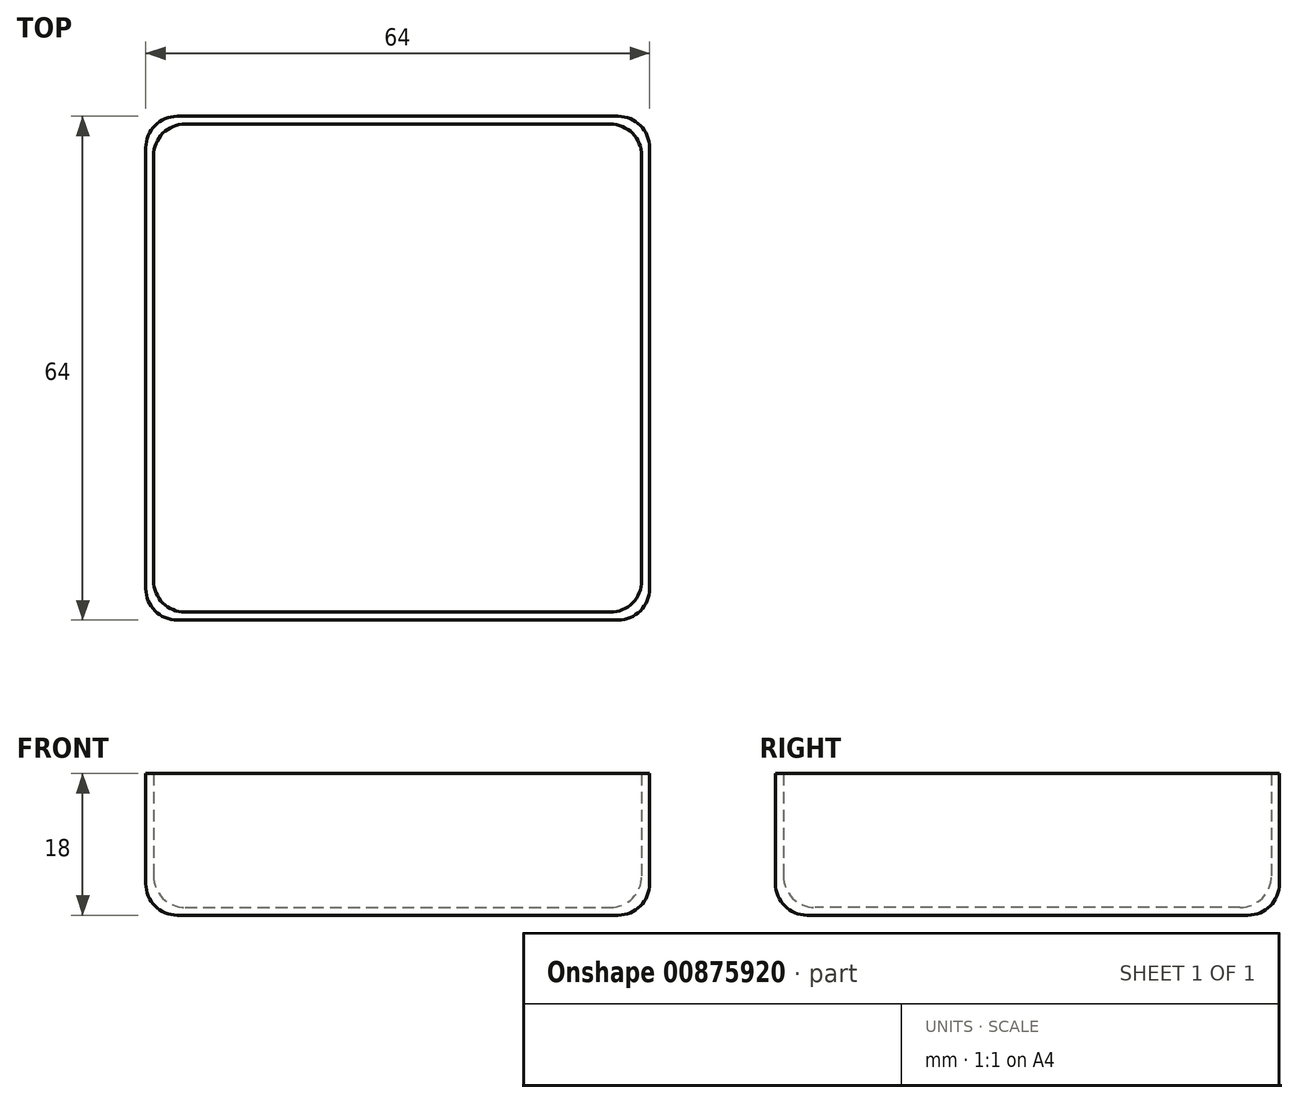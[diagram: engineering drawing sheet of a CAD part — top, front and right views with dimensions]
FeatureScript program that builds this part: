
annotation { "Feature Type Name" : "Feature", "Feature Type Description" : "" }
export const myFeature = defineFeature(function(context is Context, id is Id, definition is map)
    precondition{}
    {
        {
            assignVariable(context, id + "F0", {"name" : "wall", "anyValue" : 1});
        }
        {
            assignVariable(context, id + "F1", {"name" : "radius", "anyValue" : 4});
        }
        {
            var Q0;
            Q0=qCreatedBy(makeId("Top.planeOp"),FACE);
            var sketch = newSketch(context, id + "F2", { "sketchPlane" : qUnion([Q0])});
            skLineSegment(sketch, "E0.bottom", {"start": v(0, 0) * mm, "end": v(62, 0) * mm});
            skLineSegment(sketch, "E0.top", {"start": v(0, -62) * mm, "end": v(62, -62) * mm});
            skLineSegment(sketch, "E0.left", {"start": v(0, 0) * mm, "end": v(0, -62) * mm});
            skLineSegment(sketch, "E0.right", {"start": v(62, 0) * mm, "end": v(62, -62) * mm});
            skLineSegment(sketch, "E1.0", {"start": v(-1, 1) * mm, "end": v(-1, -63) * mm});
            skLineSegment(sketch, "E1.1", {"start": v(-1, 1) * mm, "end": v(63, 1) * mm});
            skLineSegment(sketch, "E1.2", {"start": v(63, 1) * mm, "end": v(63, -63) * mm});
            skLineSegment(sketch, "E1.3", {"start": v(-1, -63) * mm, "end": v(63, -63) * mm});
            skSolve(sketch);
        }
        {
            var Q0;
            Q0=makeQuery(id+"F2.imprint","IMPRINT",FACE,{"disambiguationData":[TD([[makeQuery(id+"F2.imprint","IMPRINT",EDGE,{"derivedFrom":sQuery(id+"F2.wireOp",EDGE,"E0.bottom")}),1.0]])]});
            var Q1;
            Q1=sQuery(id+"F2.wireOp",EDGE,"E0.right");
            var Q2;
            Q2=sQuery(id+"F2.wireOp",EDGE,"E0.left");
            var Q3;
            Q3=sQuery(id+"F2.wireOp",EDGE,"E0.bottom");
            var Q4;
            Q4=sQuery(id+"F2.wireOp",EDGE,"E0.top");
            extrude(context, id + "F3", {"entities" : qUnion([Q0]), "surfaceEntities" : qUnion([Q1, Q2, Q3, Q4]), "depth" : (18 - getVariable(context, 'wall')) * mm, "offsetDistance" : 25 * mm});
        }
        {
            var Q0;
            Q0=makeQuery(id+"F2.imprint","IMPRINT",FACE,{"disambiguationData":[TD([[makeQuery(id+"F2.imprint","IMPRINT",EDGE,{"derivedFrom":sQuery(id+"F2.wireOp",EDGE,"E0.bottom")}),-1.0]])]});
            var Q1;
            Q1=makeQuery(id+"F2.imprint","IMPRINT",FACE,{"disambiguationData":[TD([[makeQuery(id+"F2.imprint","IMPRINT",EDGE,{"derivedFrom":sQuery(id+"F2.wireOp",EDGE,"E0.bottom")}),1.0]])]});
            extrude(context, id + "F4", {"entities" : qUnion([Q0, Q1]), "operationType" : NewBodyOperationType.ADD, "oppositeDirection" : true, "depth" : (getVariable(context, 'wall')) * mm, "offsetDistance" : 25 * mm});
        }
        {
            var Q0;
            Q0=makeQuery(id+"F4.opExtrude","CAP_FACE",FACE,{"disambiguationData":[OSD([sQuery(id+"F2.wireOp",EDGE,"E1.0"),sQuery(id+"F2.wireOp",EDGE,"E1.1"),sQuery(id+"F2.wireOp",EDGE,"E1.2"),sQuery(id+"F2.wireOp",EDGE,"E1.3")])],"isStart":true});
            var Q1;
            Q1=makeQuery(id+"F4.opExtrude","CAP_FACE",FACE,{"disambiguationData":[OSD([sQuery(id+"F2.wireOp",EDGE,"E1.0"),sQuery(id+"F2.wireOp",EDGE,"E1.1"),sQuery(id+"F2.wireOp",EDGE,"E1.2"),sQuery(id+"F2.wireOp",EDGE,"E1.3")])],"isStart":false});
            var Q2;
            Q2=makeQuery(id+"F3.opExtrude","SWEPT_EDGE",EDGE,{"disambiguationData":[OSD([sQuery(id+"F2.wireOp",EDGE,"E0.top"),sQuery(id+"F2.wireOp",EDGE,"E0.left")])]});
            var Q3;
            Q3=makeQuery(id+"F3.opExtrude","SWEPT_EDGE",EDGE,{"disambiguationData":[OSD([sQuery(id+"F2.wireOp",EDGE,"E0.bottom"),sQuery(id+"F2.wireOp",EDGE,"E0.left")])]});
            var Q4;
            Q4=makeQuery(id+"F3.opExtrude","SWEPT_EDGE",EDGE,{"disambiguationData":[OSD([sQuery(id+"F2.wireOp",EDGE,"E0.bottom"),sQuery(id+"F2.wireOp",EDGE,"E0.right")])]});
            var Q5;
            Q5=makeQuery(id+"F3.opExtrude","SWEPT_EDGE",EDGE,{"disambiguationData":[OSD([sQuery(id+"F2.wireOp",EDGE,"E0.top"),sQuery(id+"F2.wireOp",EDGE,"E0.right")])]});
            var Q6;
            {var subQ0=sQuery(id+"F2.wireOp",EDGE,"E1.1");var subQ1=sQuery(id+"F2.wireOp",EDGE,"E1.0");Q6=makeQuery(id+"F4.boolean.opBoolean","MERGE",EDGE,{"derivedFrom":[makeQuery(id+"F3.opExtrude","SWEPT_EDGE",EDGE,{"disambiguationData":[OSD([subQ1,subQ0])]}),makeQuery(id+"F4.opExtrude","SWEPT_EDGE",EDGE,{"disambiguationData":[OSD([subQ1,subQ0])]})]});}
            var Q7;
            {var subQ0=sQuery(id+"F2.wireOp",EDGE,"E1.2");var subQ1=sQuery(id+"F2.wireOp",EDGE,"E1.1");Q7=makeQuery(id+"F4.boolean.opBoolean","MERGE",EDGE,{"derivedFrom":[makeQuery(id+"F3.opExtrude","SWEPT_EDGE",EDGE,{"disambiguationData":[OSD([subQ1,subQ0])]}),makeQuery(id+"F4.opExtrude","SWEPT_EDGE",EDGE,{"disambiguationData":[OSD([subQ1,subQ0])]})]});}
            var Q8;
            {var subQ0=sQuery(id+"F2.wireOp",EDGE,"E1.3");var subQ1=sQuery(id+"F2.wireOp",EDGE,"E1.2");Q8=makeQuery(id+"F4.boolean.opBoolean","MERGE",EDGE,{"derivedFrom":[makeQuery(id+"F3.opExtrude","SWEPT_EDGE",EDGE,{"disambiguationData":[OSD([subQ1,subQ0])]}),makeQuery(id+"F4.opExtrude","SWEPT_EDGE",EDGE,{"disambiguationData":[OSD([subQ1,subQ0])]})]});}
            var Q9;
            {var subQ0=sQuery(id+"F2.wireOp",EDGE,"E1.3");var subQ1=sQuery(id+"F2.wireOp",EDGE,"E1.0");Q9=makeQuery(id+"F4.boolean.opBoolean","MERGE",EDGE,{"derivedFrom":[makeQuery(id+"F3.opExtrude","SWEPT_EDGE",EDGE,{"disambiguationData":[OSD([subQ1,subQ0])]}),makeQuery(id+"F4.opExtrude","SWEPT_EDGE",EDGE,{"disambiguationData":[OSD([subQ1,subQ0])]})]});}
            fillet(context, id + "F5", {"entities" : qUnion([Q0, Q1, Q2, Q3, Q4, Q5, Q6, Q7, Q8, Q9]), "radius" : (getVariable(context, 'radius')) * mm, "tangentPropagation" : true, "allowEdgeOverflow" : false});
        }
    });
